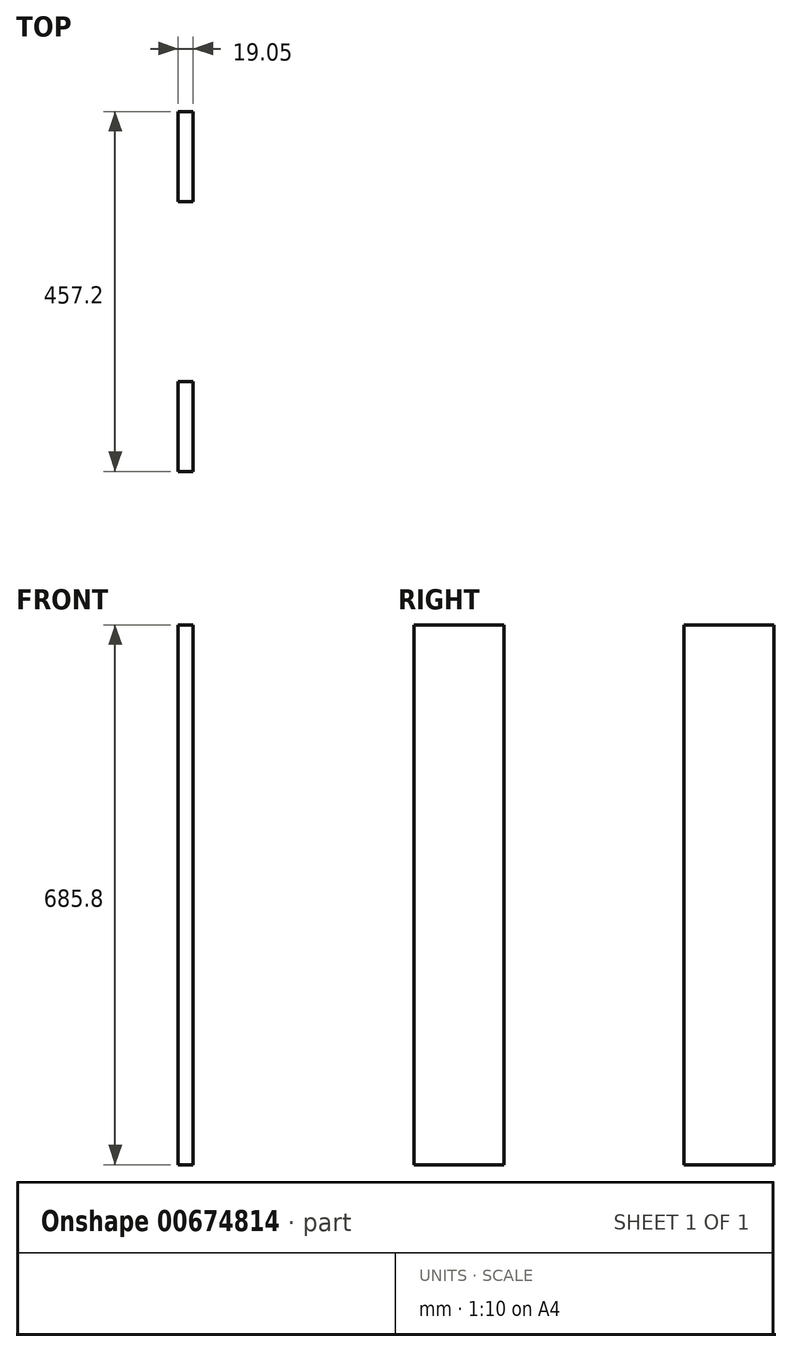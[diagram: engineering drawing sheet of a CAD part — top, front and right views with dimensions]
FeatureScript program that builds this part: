
annotation { "Feature Type Name" : "Feature", "Feature Type Description" : "" }
export const myFeature = defineFeature(function(context is Context, id is Id, definition is map)
    precondition{}
    {
        {
            var Q0;
            Q0=qCreatedBy(makeId("Right.planeOp"),FACE);
            var sketch = newSketch(context, id + "F0", { "sketchPlane" : qUnion([Q0])});
            skLineSegment(sketch, "E0.bottom", {"start": v(228.6, 342.9) * mm, "end": v(-228.6, 342.9) * mm});
            skLineSegment(sketch, "E0.top", {"start": v(228.6, -342.9) * mm, "end": v(-228.6, -342.9) * mm});
            skLineSegment(sketch, "E0.left", {"start": v(228.6, 342.9) * mm, "end": v(228.6, -342.9) * mm});
            skLineSegment(sketch, "E0.right", {"start": v(-228.6, 342.9) * mm, "end": v(-228.6, -342.9) * mm});
            skPoint(sketch, "E0.middle", {"position": v(0, 0) * mm});
            skLineSegment(sketch, "E1", {"start": v(0, 342.9) * mm, "end": v(-114.3, 342.9) * mm});
            skLineSegment(sketch, "E2", {"start": v(0, 342.9) * mm, "end": v(114.3, 342.9) * mm});
            skLineSegment(sketch, "E3", {"start": v(-114.3, 342.9) * mm, "end": v(-114.3, -342.9) * mm});
            skLineSegment(sketch, "E4", {"start": v(114.3, 342.9) * mm, "end": v(114.3, -342.9) * mm});
            skLineSegment(sketch, "E5", {"start": v(-114.3, -342.9) * mm, "end": v(-114.3, -241.3) * mm});
            skLineSegment(sketch, "E6", {"start": v(-114.3, -241.3) * mm, "end": v(114.3, -241.3) * mm});
            skSolve(sketch);
        }
        {
            var Q0;
            {var subQ1=sQuery(id+"F0.wireOp",EDGE,"E0.right");Q0=makeQuery(id+"F0.imprint","IMPRINT",FACE,{"disambiguationData":[TD([[makeQuery(id+"F0.imprint","IMPRINT",EDGE,{"derivedFrom":subQ1}),1.0]])]});}
            var Q1;
            {var subQ3=sQuery(id+"F0.wireOp",EDGE,"E5");Q1=makeQuery(id+"F0.imprint","IMPRINT",FACE,{"disambiguationData":[TD([[makeQuery(id+"F0.imprint","IMPRINT",EDGE,{"derivedFrom":subQ3}),-1.0]])]});}
            var Q2;
            {var subQ0=sQuery(id+"F0.wireOp",EDGE,"E0.left");Q2=makeQuery(id+"F0.imprint","IMPRINT",FACE,{"disambiguationData":[TD([[makeQuery(id+"F0.imprint","IMPRINT",EDGE,{"derivedFrom":subQ0}),-1.0]])]});}
            extrude(context, id + "F1", {"entities" : qUnion([Q0, Q1, Q2]), "depth" : 19.05 * mm, "offsetDistance" : 25.4 * mm});
        }
    });
